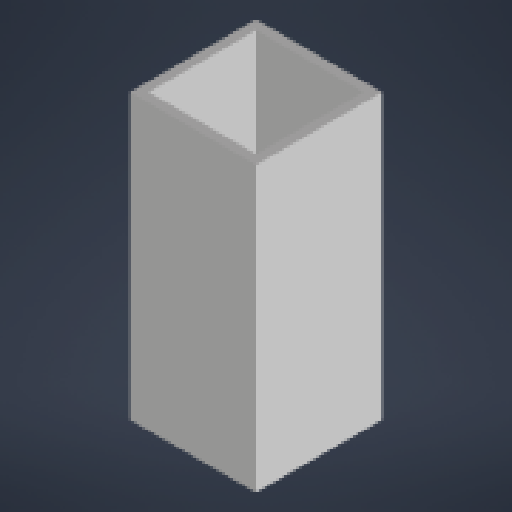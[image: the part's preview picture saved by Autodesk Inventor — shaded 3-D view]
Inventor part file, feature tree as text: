
AUTODESK INVENTOR PART (.ipt)
format: ipt  version: 2024 (Build 280153000, 153)  size: 153,600 bytes
history: native  units: mm
features: other x8, reference x7, sketch x3, extrude x3
ambient origin geometry x8: Origin, YZ Plane, XZ Plane, XY Plane, X Axis, Y Axis, Z Axis, Center Point
bodies: Body1 (feature_tree)
feature tree (21):
  other  "Твердое тело1"
  sketch  "Эскиз1"
  other  "РабПлоскость1"
  extrude  "Выдавливание1"  Depth=20.0mm
  extrude  "Выдавливание2"  Depth=1.5mm
  extrude  "Выдавливание3"  Depth=10.0mm TaperAngle=0.0deg
  reference  "Ссылка1"
  reference  "Ссылка2"
  sketch  "Эскиз2"
  reference  "Ссылка3"
  reference  "Ссылка4"
  reference  "Ссылка5"
  reference  "Ссылка6"
  sketch  "Эскиз3"
  reference  "Ссылка8"
  parser-record x1  (decoder bookkeeping rows leaked as tree rows — omitted from the tree; the rows remain in map.json)
  other  "base_assembly.iam"
  other  "square_box_section:1"
  other  "DIN 985 - заменено на DIN EN ISO 10511 M4:1"
  other  "DIN 7985 (H) M4x30-H:1"
  other  "square_box_side_section:2"
note: 1 file-system path scrubbed to <path> (originals preserved in map.json)
